# Revit family: MOR-DC-01-B_RFA
name_source: partatom
category: Aparatos sanitarios
units: mm (PartAtom-declared; Revit-internal decimal feet)

## family parameters
Activar corte en vistas = No
Compartido = No
Corte con vacíos al cargar = No
Cota de conector redondo = Usar diámetro
Mantener orientación de anotación = No
Número OmniClass = 23.45.00.00
Punto de cálculo de habitación = No
Se basa en plano de trabajo = No
Siempre vertical = Sí
Tipo de pieza = Normal
Título OmniClass = Sanitary, Laundry, and Cleaning Equipment

## types (1)
- MOR-QA-01
    Accesorios = Llave allen 5/64"
    Características = Monomando para regadera o tina sin desviador
con cartucho cerámico de 35mm.
Incluye indicador de profundidad.
    Descripción = Monomando para Regadera o Tina sin Desviador
    Diámetro = 5"
    Elevación por defecto = 47"
    Fabricante = HELVEX
    Imagen de tipo = <Ninguno>
    Instalación = Conexión interna de 1/2"-14 NPT para agua fría (azul). Conexión interna de 1/2"-14 NPT para agua caliente (rojo). Conexión interna de 1/2"-14 NPT de salida (negro).
    Material = Blanco
    Max. Working Pressure = 85.3 psi
    Min. Working Pressure = 11.4 psi
    Modelo = MOR-QA-01
    Operación = Para abrir el flujo de agua levante la palanca
y para cerrar baje la palanca. Para ajustar
la temperatura del agua, gire a la izquierda para
caliente y gire a la derecha para fría.
    Profundidad = 4"

## geometry (parser evidence)
native form markers: Sweep x3
no freeform markers — native parametric forms only
